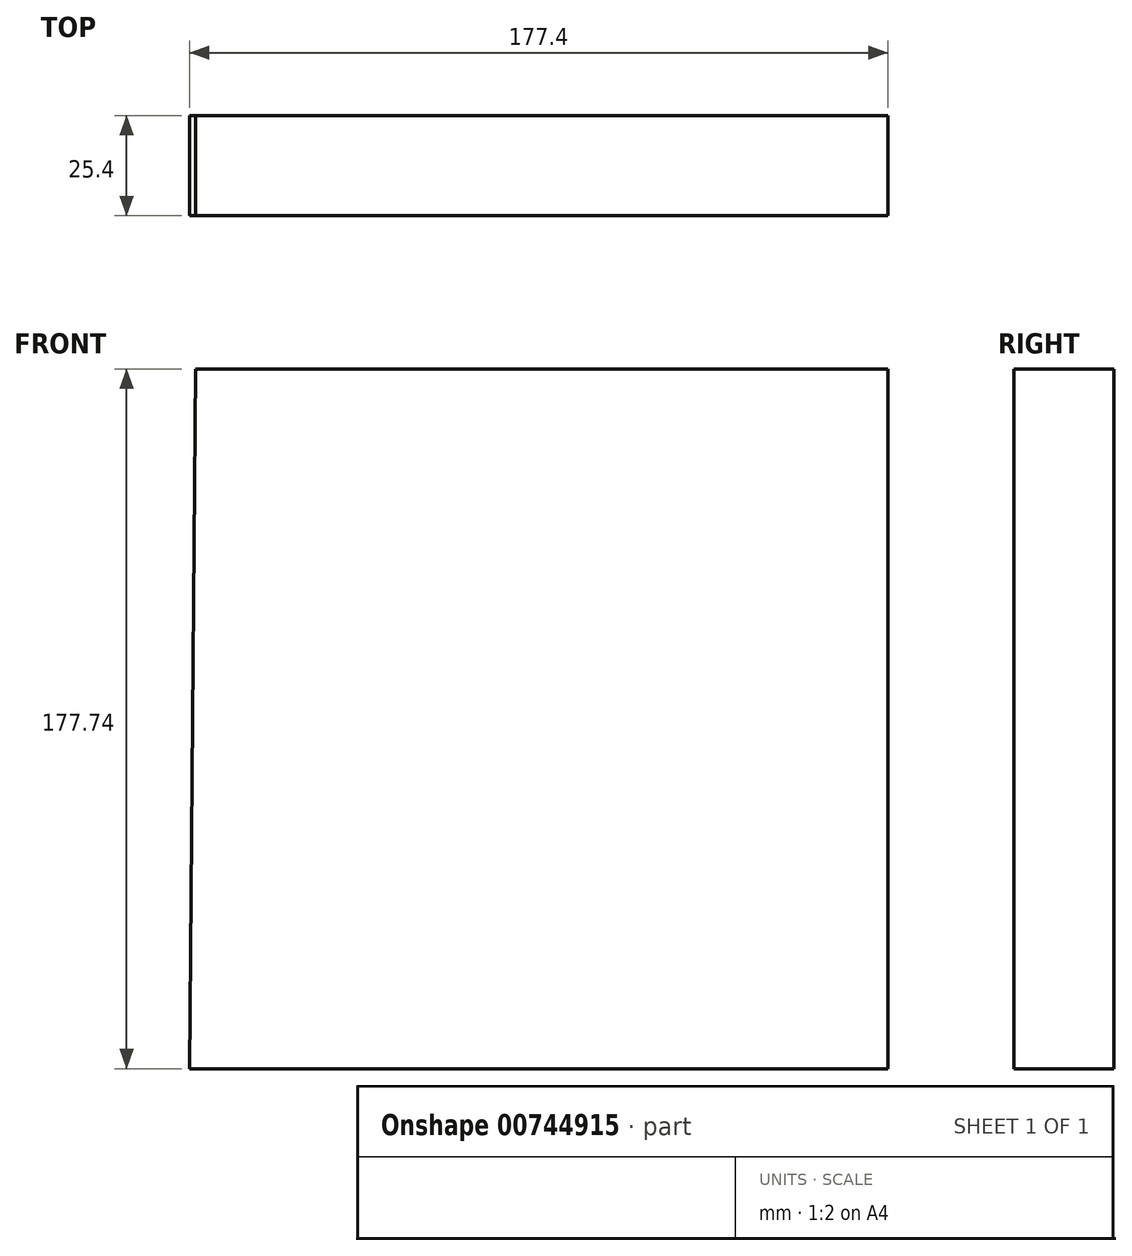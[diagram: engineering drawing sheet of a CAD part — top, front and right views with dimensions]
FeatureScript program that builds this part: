
annotation { "Feature Type Name" : "Feature", "Feature Type Description" : "" }
export const myFeature = defineFeature(function(context is Context, id is Id, definition is map)
    precondition{}
    {
        {
            var Q0;
            Q0=qCreatedBy(makeId("Front.planeOp"),FACE);
            var sketch = newSketch(context, id + "F0", { "sketchPlane" : qUnion([Q0])});
            skLineSegment(sketch, "E0", {"start": v(-86.61, 88.4) * mm, "end": v(89.24, 88.4) * mm});
            skLineSegment(sketch, "E1", {"start": v(89.24, 88.4) * mm, "end": v(89.24, -89.34) * mm});
            skLineSegment(sketch, "E2", {"start": v(89.24, -89.34) * mm, "end": v(-88.16, -89.34) * mm});
            skLineSegment(sketch, "E3", {"start": v(-88.16, -89.34) * mm, "end": v(-86.61, 88.4) * mm});
            skSolve(sketch);
        }
        {
            var Q0;
            Q0=makeQuery(id+"F0.imprint","IMPRINT",FACE,{"disambiguationData":[TD([[makeQuery(id+"F0.imprint","IMPRINT",EDGE,{"derivedFrom":sQuery(id+"F0.wireOp",EDGE,"E0")}),-1.0]])]});
            extrude(context, id + "F1", {"entities" : qUnion([Q0]), "depth" : 25.4 * mm, "offsetDistance" : 25.4 * mm});
        }
    });
